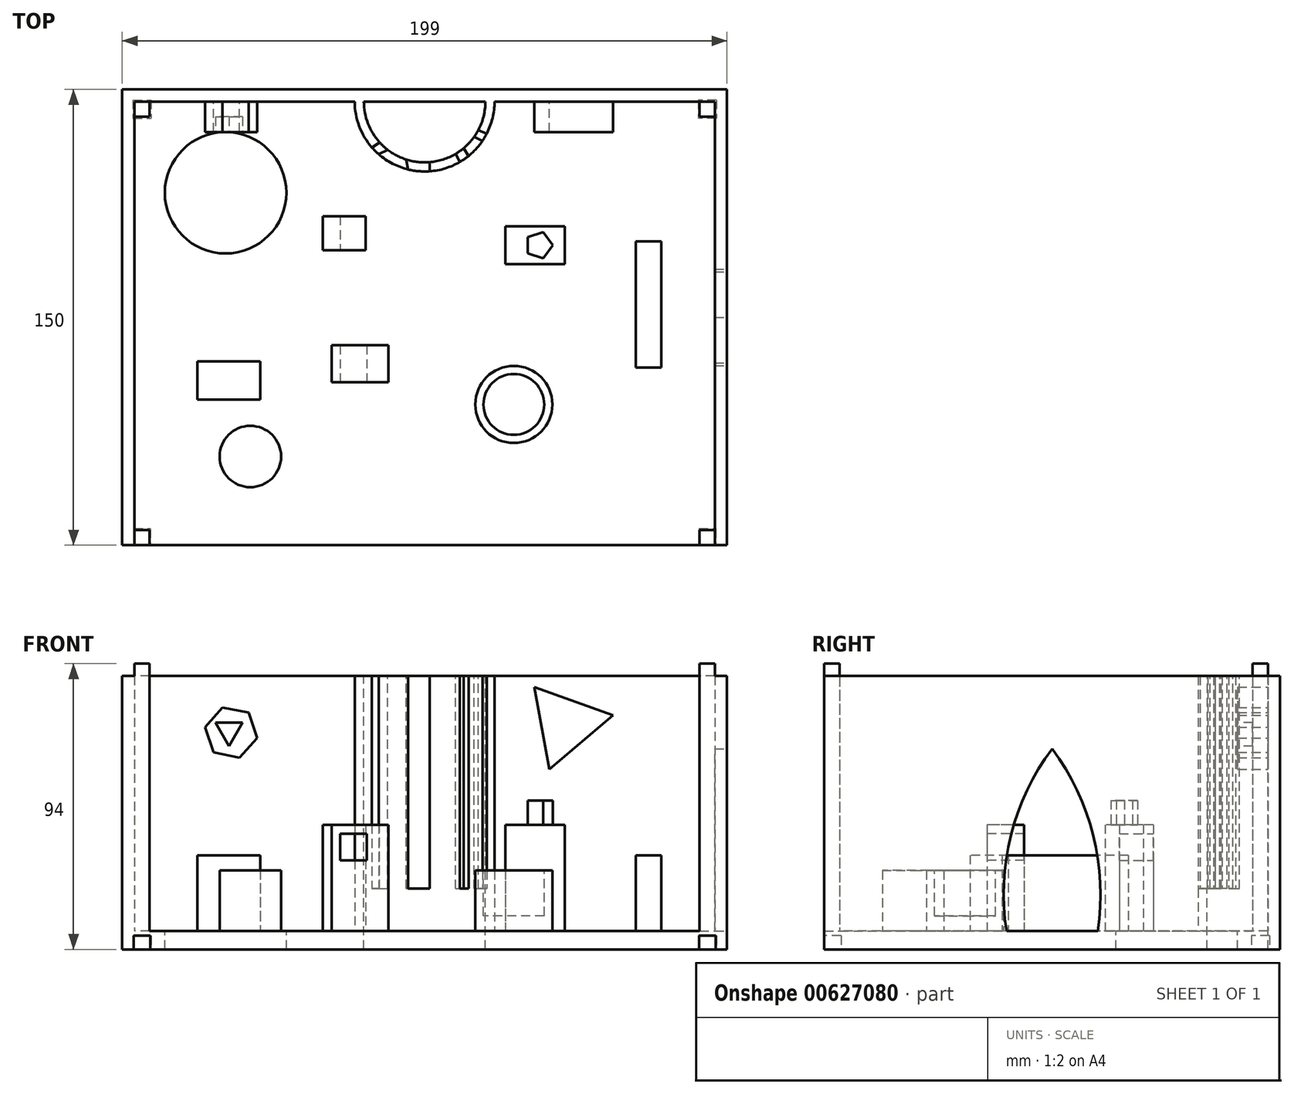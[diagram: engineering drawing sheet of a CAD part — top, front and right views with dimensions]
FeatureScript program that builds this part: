
annotation { "Feature Type Name" : "Feature", "Feature Type Description" : "" }
export const myFeature = defineFeature(function(context is Context, id is Id, definition is map)
    precondition{}
    {
        {
            var Q0;
            Q0=qCreatedBy(makeId("Top.planeOp"),FACE);
            var sketch = newSketch(context, id + "F0", { "sketchPlane" : qUnion([Q0])});
            skLineSegment(sketch, "E0.bottom", {"start": v(-99.5, 75) * mm, "end": v(99.5, 75) * mm});
            skLineSegment(sketch, "E0.top", {"start": v(-99.5, -75) * mm, "end": v(99.5, -75) * mm});
            skLineSegment(sketch, "E0.left", {"start": v(-99.5, 75) * mm, "end": v(-99.5, -75) * mm});
            skLineSegment(sketch, "E0.right", {"start": v(99.5, 75) * mm, "end": v(99.5, -75) * mm});
            skPoint(sketch, "E0.middle", {"position": v(0, 0) * mm});
            skPoint(sketch, "E1.orphan", {"position": v(-95.5, -75) * mm});
            skPoint(sketch, "E2.orphan", {"position": v(-99.5, -71) * mm});
            skPoint(sketch, "E3.orphan", {"position": v(95.5, -75) * mm});
            skPoint(sketch, "E4.orphan", {"position": v(99.5, 71) * mm});
            skPoint(sketch, "E5.orphan", {"position": v(-99.5, 71) * mm});
            skLineSegment(sketch, "E6", {"start": v(90.5, 71) * mm, "end": v(-90.5, 71) * mm});
            skLineSegment(sketch, "E7", {"start": v(-95.5, 66) * mm, "end": v(-95.5, -66) * mm});
            skLineSegment(sketch, "E8.MirrorCS", {"start": v(95.5, 66) * mm, "end": v(95.5, -66) * mm});
            skLineSegment(sketch, "E9", {"start": v(-90.5, 71) * mm, "end": v(-90.5, 66) * mm});
            skLineSegment(sketch, "E10", {"start": v(-90.5, 66) * mm, "end": v(-95.5, 66) * mm});
            skPoint(sketch, "E11.orphan", {"position": v(-95.5, 71) * mm});
            skLineSegment(sketch, "E12.MirrorCS", {"start": v(90.5, 71) * mm, "end": v(90.5, 66) * mm});
            skLineSegment(sketch, "E13.MirrorCS", {"start": v(90.5, 66) * mm, "end": v(95.5, 66) * mm});
            skLineSegment(sketch, "E14.trimOffspring", {"start": v(-95.5, -70) * mm, "end": v(-95.5, -75) * mm});
            skLineSegment(sketch, "E15.trimOffspring", {"start": v(95.5, -71) * mm, "end": v(95.5, -75) * mm});
            skPoint(sketch, "E16.orphan", {"position": v(95.5, 71) * mm});
            skLineSegment(sketch, "E17", {"start": v(-95.5, -75) * mm, "end": v(-90.5, -75) * mm});
            skLineSegment(sketch, "E18", {"start": v(-90.5, -75) * mm, "end": v(-90.5, -70) * mm});
            skLineSegment(sketch, "E19", {"start": v(-90.5, -70) * mm, "end": v(-95.5, -70) * mm});
            skLineSegment(sketch, "E20", {"start": v(-95.5, -66) * mm, "end": v(-95.5, -70) * mm});
            skLineSegment(sketch, "E21", {"start": v(-95.5, 66) * mm, "end": v(-95.5, 71) * mm});
            skLineSegment(sketch, "E22", {"start": v(-90.5, 71) * mm, "end": v(-95.5, 71) * mm});
            skLineSegment(sketch, "E23", {"start": v(90.5, 71) * mm, "end": v(95.5, 71) * mm});
            skLineSegment(sketch, "E24", {"start": v(95.5, 66) * mm, "end": v(95.5, 71) * mm});
            skLineSegment(sketch, "E25", {"start": v(95.5, -71) * mm, "end": v(95.5, -66) * mm});
            skLineSegment(sketch, "E26.MirrorCS", {"start": v(90.5, -70) * mm, "end": v(95.5, -70) * mm});
            skLineSegment(sketch, "E27.MirrorCS", {"start": v(90.5, -75) * mm, "end": v(90.5, -70) * mm});
            skSolve(sketch);
        }
        {
            var Q0;
            Q0=makeQuery(id+"F0.imprint","IMPRINT",FACE,{"disambiguationData":[TD([[makeQuery(id+"F0.imprint","IMPRINT",EDGE,{"derivedFrom":sQuery(id+"F0.wireOp",EDGE,"E6")}),1.0]])]});
            var Q1;
            Q1=makeQuery(id+"F0.imprint","IMPRINT",FACE,{"disambiguationData":[TD([[makeQuery(id+"F0.imprint","IMPRINT",EDGE,{"derivedFrom":sQuery(id+"F0.wireOp",EDGE,"E0.bottom")}),-1.0]])]});
            extrude(context, id + "F1", {"entities" : qUnion([Q0, Q1]), "depth" : 6 * mm, "offsetDistance" : 25 * mm});
        }
        {
            var Q0;
            Q0=makeQuery(id+"F0.imprint","IMPRINT",FACE,{"disambiguationData":[TD([[makeQuery(id+"F0.imprint","IMPRINT",EDGE,{"derivedFrom":sQuery(id+"F0.wireOp",EDGE,"E0.bottom")}),-1.0]])]});
            extrude(context, id + "F2", {"entities" : qUnion([Q0]), "operationType" : NewBodyOperationType.ADD, "depth" : 90 * mm, "offsetDistance" : 25 * mm});
        }
        {
            var Q0;
            Q0=makeQuery(id+"F0.imprint","IMPRINT",FACE,{"disambiguationData":[TD([[makeQuery(id+"F0.imprint","IMPRINT",EDGE,{"derivedFrom":sQuery(id+"F0.wireOp",EDGE,"E9")}),-1.0]])]});
            var Q1;
            Q1=makeQuery(id+"F0.imprint","IMPRINT",FACE,{"disambiguationData":[TD([[makeQuery(id+"F0.imprint","IMPRINT",EDGE,{"derivedFrom":sQuery(id+"F0.wireOp",EDGE,"E12.MirrorCS")}),1.0]])]});
            var Q2;
            {var subQ1=sQuery(id+"F0.wireOp",EDGE,"E15.trimOffspring");Q2=makeQuery(id+"F0.imprint","IMPRINT",FACE,{"disambiguationData":[TD([[makeQuery(id+"F0.imprint","IMPRINT",EDGE,{"derivedFrom":subQ1}),-1.0]])]});}
            var Q3;
            Q3=makeQuery(id+"F0.imprint","IMPRINT",FACE,{"disambiguationData":[TD([[makeQuery(id+"F0.imprint","IMPRINT",EDGE,{"derivedFrom":sQuery(id+"F0.wireOp",EDGE,"E14.trimOffspring")}),1.0]])]});
            extrude(context, id + "F3", {"entities" : qUnion([Q0, Q1, Q2, Q3]), "operationType" : NewBodyOperationType.ADD, "depth" : 94 * mm, "offsetDistance" : 25 * mm});
        }
        {
            var Q0;
            {var subQ0=sQuery(id+"F0.wireOp",EDGE,"E17");var subQ1=sQuery(id+"F0.wireOp",EDGE,"E0.top");var subQ2=makeQuery(id+"F0.imprint","IMPRINT",EDGE,{"disambiguationData":[TD([[makeQuery(id+"F0.imprint","INTERSECT",VERTEX,{"derivedFrom":[subQ1,sQuery(id+"F0.wireOp",EDGE,"E0.right")]}),1.0]])],"derivedFrom":subQ1});var subQ3=makeQuery(id+"F0.imprint","IMPRINT",EDGE,{"disambiguationData":[TD([[makeQuery(id+"F0.imprint","INTERSECT",VERTEX,{"derivedFrom":[subQ1,sQuery(id+"F0.wireOp",EDGE,"E0.left")]}),-1.0]])],"derivedFrom":subQ1});Q0=makeQuery(id+"F3.boolean.opBoolean","MERGE",FACE,{"derivedFrom":[makeQuery(id+"F1.opExtrude","SWEPT_FACE",FACE,{"disambiguationData":[OSD([subQ1]),TDD([makeQuery(id+"F0.imprint","IMPRINT",EDGE,{"disambiguationData":[TD([[makeQuery(id+"F0.imprint","INTERSECT",VERTEX,{"derivedFrom":[subQ1,sQuery(id+"F0.wireOp",EDGE,"E27.MirrorCS")]}),1.0]])],"derivedFrom":subQ1})])]}),makeQuery(id+"F2.boolean.opBoolean","MERGE",FACE,{"derivedFrom":[makeQuery(id+"F1.opExtrude","SWEPT_FACE",FACE,{"disambiguationData":[OSD([subQ1]),TDD([subQ3])]}),makeQuery(id+"F2.opExtrude","SWEPT_FACE",FACE,{"disambiguationData":[OSD([subQ1]),TDD([subQ3])]})]}),makeQuery(id+"F2.boolean.opBoolean","MERGE",FACE,{"derivedFrom":[makeQuery(id+"F1.opExtrude","SWEPT_FACE",FACE,{"disambiguationData":[OSD([subQ1]),TDD([subQ2])]}),makeQuery(id+"F2.opExtrude","SWEPT_FACE",FACE,{"disambiguationData":[OSD([subQ1]),TDD([subQ2])]})]}),makeQuery(id+"F3.opExtrude","SWEPT_FACE",FACE,{"disambiguationData":[OSD([subQ1])]}),makeQuery(id+"F3.opExtrude","SWEPT_FACE",FACE,{"disambiguationData":[OSD([subQ0])]})]});}
            var sketch = newSketch(context, id + "F4", { "sketchPlane" : qUnion([Q0])});
            skLineSegment(sketch, "E28", {"start": v(90.25, 4.5) * mm, "end": v(90.25, 0) * mm});
            skLineSegment(sketch, "E29", {"start": v(95.75, 4.5) * mm, "end": v(95.75, 0) * mm});
            skLineSegment(sketch, "E30", {"start": v(95.75, 0) * mm, "end": v(95.75, 4.5) * mm});
            skLineSegment(sketch, "E31", {"start": v(95.75, 4.5) * mm, "end": v(90.25, 4.5) * mm});
            skLineSegment(sketch, "E32", {"start": v(95.75, 0) * mm, "end": v(90.25, 0) * mm});
            skLineSegment(sketch, "E33.MirrorCS", {"start": v(-90.25, 4.5) * mm, "end": v(-90.25, 0) * mm});
            skLineSegment(sketch, "E34.MirrorCS", {"start": v(-95.75, 4.5) * mm, "end": v(-90.25, 4.5) * mm});
            skLineSegment(sketch, "E35.MirrorCS", {"start": v(-95.75, 0) * mm, "end": v(-90.25, 0) * mm});
            skLineSegment(sketch, "E36.MirrorCS", {"start": v(-95.75, 0) * mm, "end": v(-95.75, 4.5) * mm});
            skSolve(sketch);
        }
        {
            var Q0;
            Q0=makeQuery(id+"F4.imprint","IMPRINT",FACE,{"disambiguationData":[TD([[makeQuery(id+"F4.imprint","IMPRINT",EDGE,{"derivedFrom":sQuery(id+"F4.wireOp",EDGE,"E28")}),1.0]])]});
            extrude(context, id + "F5", {"entities" : qUnion([Q0]), "operationType" : NewBodyOperationType.REMOVE, "oppositeDirection" : true, "depth" : 5.5 * mm, "offsetDistance" : 25 * mm});
        }
        {
            var Q0;
            Q0=makeQuery(id+"F4.imprint","IMPRINT",FACE,{"disambiguationData":[TD([[makeQuery(id+"F4.imprint","IMPRINT",EDGE,{"derivedFrom":sQuery(id+"F4.wireOp",EDGE,"E33.MirrorCS")}),-1.0]])]});
            extrude(context, id + "F6", {"entities" : qUnion([Q0]), "operationType" : NewBodyOperationType.REMOVE, "depth" : 5.5 * mm, "offsetDistance" : 25 * mm});
        }
        {
            var Q0;
            Q0=makeQuery(id+"F1.opExtrude","CAP_FACE",FACE,{"disambiguationData":[OSD([sQuery(id+"F0.wireOp",EDGE,"E0.bottom"),sQuery(id+"F0.wireOp",EDGE,"E0.top"),sQuery(id+"F0.wireOp",EDGE,"E0.left"),sQuery(id+"F0.wireOp",EDGE,"E0.right"),sQuery(id+"F0.wireOp",EDGE,"E9"),sQuery(id+"F0.wireOp",EDGE,"E10"),sQuery(id+"F0.wireOp",EDGE,"E12.MirrorCS"),sQuery(id+"F0.wireOp",EDGE,"E13.MirrorCS"),sQuery(id+"F0.wireOp",EDGE,"E14.trimOffspring"),sQuery(id+"F0.wireOp",EDGE,"E15.trimOffspring"),sQuery(id+"F0.wireOp",EDGE,"E18"),sQuery(id+"F0.wireOp",EDGE,"E19"),sQuery(id+"F0.wireOp",EDGE,"E21"),sQuery(id+"F0.wireOp",EDGE,"E22"),sQuery(id+"F0.wireOp",EDGE,"E23"),sQuery(id+"F0.wireOp",EDGE,"E24"),sQuery(id+"F0.wireOp",EDGE,"E25"),sQuery(id+"F0.wireOp",EDGE,"E26.MirrorCS"),sQuery(id+"F0.wireOp",EDGE,"E27.MirrorCS")])],"isStart":false});
            var sketch = newSketch(context, id + "F7", { "sketchPlane" : qUnion([Q0])});
            skLineSegment(sketch, "E37", {"start": v(-90.5, 71) * mm, "end": v(-85.5, 71) * mm});
            skCircle(sketch, "E38", {"center": v(-65.5, 41) * mm, "radius": 20 * mm});
            skArc(sketch, "E39", {"start": v(-20, 71) * mm, "mid": v(0, 51) * mm, "end": v(20, 71) * mm});
            skLineSegment(sketch, "E40", {"start": v(20, 71) * mm, "end": v(-20, 71) * mm});
            skArc(sketch, "E41", {"start": v(-23, 71) * mm, "mid": v(0, 48) * mm, "end": v(23, 71) * mm});
            skLineSegment(sketch, "E42", {"start": v(23, 71) * mm, "end": v(-23, 71) * mm});
            skSolve(sketch);
        }
        {
            var Q0;
            Q0=makeQuery(id+"F7.imprint","IMPRINT",FACE,{"disambiguationData":[TD([[makeQuery(id+"F7.imprint","IMPRINT",EDGE,{"derivedFrom":sQuery(id+"F7.wireOp",EDGE,"E38")}),1.0]])]});
            extrude(context, id + "F8", {"entities" : qUnion([Q0]), "operationType" : NewBodyOperationType.REMOVE, "oppositeDirection" : true, "depth" : 7 * mm, "offsetDistance" : 25 * mm});
        }
        {
            var Q0;
            {var subQ0=sQuery(id+"F7.wireOp",EDGE,"E39");Q0=makeQuery(id+"F7.imprint","IMPRINT",FACE,{"disambiguationData":[TD([[makeQuery(id+"F7.imprint","IMPRINT",EDGE,{"derivedFrom":subQ0}),1.0]])]});}
            extrude(context, id + "F9", {"entities" : qUnion([Q0]), "operationType" : NewBodyOperationType.REMOVE, "oppositeDirection" : true, "depth" : 6 * mm, "offsetDistance" : 25 * mm});
        }
        {
            var Q0;
            {var subQ0=sQuery(id+"F7.wireOp",EDGE,"E39");Q0=makeQuery(id+"F7.imprint","IMPRINT",FACE,{"disambiguationData":[TD([[makeQuery(id+"F7.imprint","IMPRINT",EDGE,{"derivedFrom":subQ0}),-1.0]])]});}
            extrude(context, id + "F10", {"entities" : qUnion([Q0]), "operationType" : NewBodyOperationType.ADD, "depth" : 84 * mm, "offsetDistance" : 25 * mm});
        }
        {
            var Q0;
            {var subQ0=sQuery(id+"F0.wireOp",EDGE,"E0.right");Q0=makeQuery(id+"F2.boolean.opBoolean","MERGE",FACE,{"derivedFrom":[makeQuery(id+"F1.opExtrude","SWEPT_FACE",FACE,{"disambiguationData":[OSD([subQ0])]}),makeQuery(id+"F2.opExtrude","SWEPT_FACE",FACE,{"disambiguationData":[OSD([subQ0])]})]});}
            var sketch = newSketch(context, id + "F11", { "sketchPlane" : qUnion([Q0])});
            skLineSegment(sketch, "E43", {"start": v(14.97, 6) * mm, "end": v(-15.03, 6) * mm});
            skArc(sketch, "E44", {"start": v(-0.03, 66) * mm, "mid": v(-13.58, 37.51) * mm, "end": v(-15.03, 6) * mm});
            skArc(sketch, "E45.MirrorCS", {"start": v(-0.03, 66) * mm, "mid": v(13.52, 37.51) * mm, "end": v(14.97, 6) * mm});
            skSolve(sketch);
        }
        {
            var Q0;
            Q0=makeQuery(id+"F11.imprint","IMPRINT",FACE,{"disambiguationData":[TD([[makeQuery(id+"F11.imprint","IMPRINT",EDGE,{"derivedFrom":sQuery(id+"F11.wireOp",EDGE,"E43")}),-1.0]])]});
            extrude(context, id + "F12", {"entities" : qUnion([Q0]), "operationType" : NewBodyOperationType.REMOVE, "oppositeDirection" : true, "depth" : 4 * mm, "offsetDistance" : 25 * mm});
        }
        {
            var Q0;
            Q0=makeQuery(id+"F4.imprint","IMPRINT",FACE,{"disambiguationData":[TD([[makeQuery(id+"F4.imprint","IMPRINT",EDGE,{"derivedFrom":sQuery(id+"F4.wireOp",EDGE,"E33.MirrorCS")}),-1.0]])]});
            extrude(context, id + "F13", {"entities" : qUnion([Q0]), "operationType" : NewBodyOperationType.REMOVE, "oppositeDirection" : true, "depth" : 5.5 * mm, "offsetDistance" : 25 * mm});
        }
        {
            var Q0;
            Q0=makeQuery(id+"F0.imprint","IMPRINT",FACE,{"disambiguationData":[TD([[makeQuery(id+"F0.imprint","IMPRINT",EDGE,{"derivedFrom":sQuery(id+"F0.wireOp",EDGE,"E9")}),-1.0]])]});
            extrude(context, id + "F14", {"entities" : qUnion([Q0]), "operationType" : NewBodyOperationType.ADD, "depth" : 25 * mm, "offsetDistance" : 25 * mm});
        }
        {
            var Q0;
            {var subQ0=sQuery(id+"F0.wireOp",EDGE,"E19");var subQ1=sQuery(id+"F0.wireOp",EDGE,"E18");var subQ2=sQuery(id+"F0.wireOp",EDGE,"E14.trimOffspring");var subQ3=sQuery(id+"F0.wireOp",EDGE,"E24");var subQ4=sQuery(id+"F0.wireOp",EDGE,"E23");var subQ5=sQuery(id+"F0.wireOp",EDGE,"E13.MirrorCS");var subQ6=sQuery(id+"F0.wireOp",EDGE,"E12.MirrorCS");var subQ7=sQuery(id+"F0.wireOp",EDGE,"E22");var subQ8=sQuery(id+"F0.wireOp",EDGE,"E21");var subQ9=sQuery(id+"F0.wireOp",EDGE,"E10");var subQ10=sQuery(id+"F0.wireOp",EDGE,"E9");var subQ11=sQuery(id+"F0.wireOp",EDGE,"E27.MirrorCS");var subQ12=sQuery(id+"F0.wireOp",EDGE,"E26.MirrorCS");var subQ13=sQuery(id+"F0.wireOp",EDGE,"E25");var subQ14=sQuery(id+"F0.wireOp",EDGE,"E15.trimOffspring");var subQ15=sQuery(id+"F0.wireOp",EDGE,"E0.top");Q0=makeQuery(id+"F3.boolean.opBoolean","MERGE",FACE,{"derivedFrom":[makeQuery(id+"F1.opExtrude","CAP_FACE",FACE,{"disambiguationData":[OSD([sQuery(id+"F0.wireOp",EDGE,"E0.bottom"),subQ15,sQuery(id+"F0.wireOp",EDGE,"E0.left"),sQuery(id+"F0.wireOp",EDGE,"E0.right"),subQ10,subQ9,subQ6,subQ5,subQ2,subQ14,subQ1,subQ0,subQ8,subQ7,subQ4,subQ3,subQ13,subQ12,subQ11])],"isStart":true}),makeQuery(id+"F3.opExtrude","CAP_FACE",FACE,{"disambiguationData":[OSD([subQ15,subQ14,subQ13,subQ12,subQ11])],"isStart":true}),makeQuery(id+"F3.opExtrude","CAP_FACE",FACE,{"disambiguationData":[OSD([subQ10,subQ9,subQ8,subQ7])],"isStart":true}),makeQuery(id+"F3.opExtrude","CAP_FACE",FACE,{"disambiguationData":[OSD([subQ6,subQ5,subQ4,subQ3])],"isStart":true}),makeQuery(id+"F3.opExtrude","CAP_FACE",FACE,{"disambiguationData":[OSD([subQ2,sQuery(id+"F0.wireOp",EDGE,"E17"),subQ1,subQ0])],"isStart":true})]});}
            var sketch = newSketch(context, id + "F15", { "sketchPlane" : qUnion([Q0])});
            skLineSegment(sketch, "E46.0", {"start": v(-96, -71.49) * mm, "end": v(-96, -65.49) * mm});
            skLineSegment(sketch, "E46.1", {"start": v(-96, -71.49) * mm, "end": v(-90, -71.49) * mm});
            skLineSegment(sketch, "E46.2", {"start": v(-90, -71.49) * mm, "end": v(-90, -65.49) * mm});
            skLineSegment(sketch, "E46.3", {"start": v(-96, -65.49) * mm, "end": v(-90, -65.49) * mm});
            skSolve(sketch);
        }
        {
            var Q0;
            Q0=makeQuery(id+"F15.imprint","IMPRINT",FACE,{"disambiguationData":[TD([[makeQuery(id+"F15.imprint","IMPRINT",EDGE,{"derivedFrom":sQuery(id+"F15.wireOp",EDGE,"E46.0")}),-1.0]])]});
            extrude(context, id + "F16", {"entities" : qUnion([Q0]), "operationType" : NewBodyOperationType.REMOVE, "oppositeDirection" : true, "depth" : 4.5 * mm, "offsetDistance" : 25 * mm});
        }
        {
            var Q0;
            {var subQ0=sQuery(id+"F0.wireOp",EDGE,"E19");var subQ1=sQuery(id+"F0.wireOp",EDGE,"E18");var subQ2=sQuery(id+"F0.wireOp",EDGE,"E14.trimOffspring");var subQ3=sQuery(id+"F0.wireOp",EDGE,"E24");var subQ4=sQuery(id+"F0.wireOp",EDGE,"E23");var subQ5=sQuery(id+"F0.wireOp",EDGE,"E13.MirrorCS");var subQ6=sQuery(id+"F0.wireOp",EDGE,"E12.MirrorCS");var subQ7=sQuery(id+"F0.wireOp",EDGE,"E22");var subQ8=sQuery(id+"F0.wireOp",EDGE,"E21");var subQ9=sQuery(id+"F0.wireOp",EDGE,"E10");var subQ10=sQuery(id+"F0.wireOp",EDGE,"E9");var subQ11=sQuery(id+"F0.wireOp",EDGE,"E27.MirrorCS");var subQ12=sQuery(id+"F0.wireOp",EDGE,"E26.MirrorCS");var subQ13=sQuery(id+"F0.wireOp",EDGE,"E25");var subQ14=sQuery(id+"F0.wireOp",EDGE,"E15.trimOffspring");var subQ15=sQuery(id+"F0.wireOp",EDGE,"E0.top");Q0=makeQuery(id+"F3.boolean.opBoolean","MERGE",FACE,{"derivedFrom":[makeQuery(id+"F1.opExtrude","CAP_FACE",FACE,{"disambiguationData":[OSD([sQuery(id+"F0.wireOp",EDGE,"E0.bottom"),subQ15,sQuery(id+"F0.wireOp",EDGE,"E0.left"),sQuery(id+"F0.wireOp",EDGE,"E0.right"),subQ10,subQ9,subQ6,subQ5,subQ2,subQ14,subQ1,subQ0,subQ8,subQ7,subQ4,subQ3,subQ13,subQ12,subQ11])],"isStart":true}),makeQuery(id+"F3.opExtrude","CAP_FACE",FACE,{"disambiguationData":[OSD([subQ15,subQ14,subQ13,subQ12,subQ11])],"isStart":true}),makeQuery(id+"F3.opExtrude","CAP_FACE",FACE,{"disambiguationData":[OSD([subQ10,subQ9,subQ8,subQ7])],"isStart":true}),makeQuery(id+"F3.opExtrude","CAP_FACE",FACE,{"disambiguationData":[OSD([subQ6,subQ5,subQ4,subQ3])],"isStart":true}),makeQuery(id+"F3.opExtrude","CAP_FACE",FACE,{"disambiguationData":[OSD([subQ2,sQuery(id+"F0.wireOp",EDGE,"E17"),subQ1,subQ0])],"isStart":true})]});}
            var sketch = newSketch(context, id + "F17", { "sketchPlane" : qUnion([Q0])});
            skLineSegment(sketch, "E47.0", {"start": v(96, -65.5) * mm, "end": v(90, -65.5) * mm});
            skLineSegment(sketch, "E47.1", {"start": v(96, -71.5) * mm, "end": v(96, -65.5) * mm});
            skLineSegment(sketch, "E47.2", {"start": v(96, -71.5) * mm, "end": v(90, -71.5) * mm});
            skLineSegment(sketch, "E47.3", {"start": v(90, -71.5) * mm, "end": v(90, -65.5) * mm});
            skSolve(sketch);
        }
        {
            var Q0;
            Q0=makeQuery(id+"F17.imprint","IMPRINT",FACE,{"disambiguationData":[TD([[makeQuery(id+"F17.imprint","IMPRINT",EDGE,{"derivedFrom":sQuery(id+"F17.wireOp",EDGE,"E47.0")}),1.0]])]});
            extrude(context, id + "F18", {"entities" : qUnion([Q0]), "operationType" : NewBodyOperationType.REMOVE, "oppositeDirection" : true, "depth" : 4.5 * mm, "offsetDistance" : 25 * mm});
        }
        {
            var Q0;
            Q0=makeQuery(id+"F12.boolean.opBoolean","MERGE",FACE,{"derivedFrom":[makeQuery(id+"F1.opExtrude","CAP_FACE",FACE,{"disambiguationData":[OSD([sQuery(id+"F0.wireOp",EDGE,"E0.bottom"),sQuery(id+"F0.wireOp",EDGE,"E0.top"),sQuery(id+"F0.wireOp",EDGE,"E0.left"),sQuery(id+"F0.wireOp",EDGE,"E0.right"),sQuery(id+"F0.wireOp",EDGE,"E9"),sQuery(id+"F0.wireOp",EDGE,"E10"),sQuery(id+"F0.wireOp",EDGE,"E12.MirrorCS"),sQuery(id+"F0.wireOp",EDGE,"E13.MirrorCS"),sQuery(id+"F0.wireOp",EDGE,"E14.trimOffspring"),sQuery(id+"F0.wireOp",EDGE,"E15.trimOffspring"),sQuery(id+"F0.wireOp",EDGE,"E18"),sQuery(id+"F0.wireOp",EDGE,"E19"),sQuery(id+"F0.wireOp",EDGE,"E21"),sQuery(id+"F0.wireOp",EDGE,"E22"),sQuery(id+"F0.wireOp",EDGE,"E23"),sQuery(id+"F0.wireOp",EDGE,"E24"),sQuery(id+"F0.wireOp",EDGE,"E25"),sQuery(id+"F0.wireOp",EDGE,"E26.MirrorCS"),sQuery(id+"F0.wireOp",EDGE,"E27.MirrorCS")])],"isStart":false}),makeQuery(id+"F12.opExtrude","SWEPT_FACE",FACE,{"disambiguationData":[OSD([sQuery(id+"F11.wireOp",EDGE,"E43")])]})]});
            var sketch = newSketch(context, id + "F19", { "sketchPlane" : qUnion([Q0])});
            skLineSegment(sketch, "E48.bottom", {"start": v(26.55, 29.99) * mm, "end": v(46.13, 29.99) * mm});
            skLineSegment(sketch, "E48.top", {"start": v(26.55, 17.47) * mm, "end": v(46.13, 17.47) * mm});
            skLineSegment(sketch, "E48.left", {"start": v(26.55, 29.99) * mm, "end": v(26.55, 17.47) * mm});
            skLineSegment(sketch, "E48.right", {"start": v(46.13, 29.99) * mm, "end": v(46.13, 17.47) * mm});
            skLineSegment(sketch, "E49.bottom", {"start": v(-30.54, -9.23) * mm, "end": v(-11.9, -9.23) * mm});
            skLineSegment(sketch, "E49.top", {"start": v(-30.54, -21.42) * mm, "end": v(-11.9, -21.42) * mm});
            skLineSegment(sketch, "E49.left", {"start": v(-30.54, -9.23) * mm, "end": v(-30.54, -21.42) * mm});
            skLineSegment(sketch, "E49.right", {"start": v(-11.9, -9.23) * mm, "end": v(-11.9, -21.42) * mm});
            skLineSegment(sketch, "E50.bottom", {"start": v(-33.57, 33.29) * mm, "end": v(-19.36, 33.29) * mm});
            skLineSegment(sketch, "E50.top", {"start": v(-33.57, 22.08) * mm, "end": v(-19.36, 22.08) * mm});
            skLineSegment(sketch, "E50.left", {"start": v(-33.57, 33.29) * mm, "end": v(-33.57, 22.08) * mm});
            skLineSegment(sketch, "E50.right", {"start": v(-19.36, 33.29) * mm, "end": v(-19.36, 22.08) * mm});
            skLineSegment(sketch, "E51.bottom", {"start": v(-74.82, -14.5) * mm, "end": v(-54.08, -14.5) * mm});
            skLineSegment(sketch, "E51.top", {"start": v(-74.82, -27.02) * mm, "end": v(-54.08, -27.02) * mm});
            skLineSegment(sketch, "E51.left", {"start": v(-74.82, -14.5) * mm, "end": v(-74.82, -27.02) * mm});
            skLineSegment(sketch, "E51.right", {"start": v(-54.08, -14.5) * mm, "end": v(-54.08, -27.02) * mm});
            skLineSegment(sketch, "E52.bottom", {"start": v(69.43, 25.05) * mm, "end": v(77.82, 25.05) * mm});
            skLineSegment(sketch, "E52.top", {"start": v(69.43, -16.48) * mm, "end": v(77.82, -16.48) * mm});
            skLineSegment(sketch, "E52.left", {"start": v(69.43, 25.05) * mm, "end": v(69.43, -16.48) * mm});
            skLineSegment(sketch, "E52.right", {"start": v(77.82, 25.05) * mm, "end": v(77.82, -16.48) * mm});
            skSolve(sketch);
        }
        {
            var Q0;
            Q0=makeQuery(id+"F19.imprint","IMPRINT",FACE,{"disambiguationData":[TD([[makeQuery(id+"F19.imprint","IMPRINT",EDGE,{"derivedFrom":sQuery(id+"F19.wireOp",EDGE,"E51.bottom")}),-1.0]])]});
            var Q1;
            Q1=makeQuery(id+"F19.imprint","IMPRINT",FACE,{"disambiguationData":[TD([[makeQuery(id+"F19.imprint","IMPRINT",EDGE,{"derivedFrom":sQuery(id+"F19.wireOp",EDGE,"E52.bottom")}),-1.0]])]});
            extrude(context, id + "F20", {"entities" : qUnion([Q0, Q1]), "operationType" : NewBodyOperationType.ADD, "depth" : 25 * mm, "offsetDistance" : 25 * mm});
        }
        {
            var Q0;
            Q0=makeQuery(id+"F19.imprint","IMPRINT",FACE,{"disambiguationData":[TD([[makeQuery(id+"F19.imprint","IMPRINT",EDGE,{"derivedFrom":sQuery(id+"F19.wireOp",EDGE,"E50.bottom")}),-1.0]])]});
            var Q1;
            Q1=makeQuery(id+"F19.imprint","IMPRINT",FACE,{"disambiguationData":[TD([[makeQuery(id+"F19.imprint","IMPRINT",EDGE,{"derivedFrom":sQuery(id+"F19.wireOp",EDGE,"E49.bottom")}),-1.0]])]});
            var Q2;
            Q2=makeQuery(id+"F19.imprint","IMPRINT",FACE,{"disambiguationData":[TD([[makeQuery(id+"F19.imprint","IMPRINT",EDGE,{"derivedFrom":sQuery(id+"F19.wireOp",EDGE,"E48.bottom")}),-1.0]])]});
            extrude(context, id + "F21", {"entities" : qUnion([Q0, Q1, Q2]), "operationType" : NewBodyOperationType.ADD, "depth" : 35 * mm, "offsetDistance" : 25 * mm});
        }
        {
            var Q0;
            Q0=makeQuery(id+"F19.imprint","IMPRINT",FACE,{"disambiguationData":[TD([[makeQuery(id+"F19.imprint","IMPRINT",EDGE,{"derivedFrom":sQuery(id+"F19.wireOp",EDGE,"E48.bottom")}),1.0]])]});
            var sketch = newSketch(context, id + "F22", { "sketchPlane" : qUnion([Q0])});
            skCircle(sketch, "E53", {"center": v(29.35, -28.67) * mm, "radius": 12.68 * mm});
            skCircle(sketch, "E54", {"center": v(-57.34, -45.8) * mm, "radius": 10.1 * mm});
            skSolve(sketch);
        }
        {
            var Q0;
            Q0 = qSketchRegion(id + "F22", true);
            extrude(context, id + "F23", {"entities" : qUnion([Q0]), "operationType" : NewBodyOperationType.ADD, "depth" : 20 * mm, "offsetDistance" : 25 * mm});
        }
        {
            var Q0;
            {var subQ0=sQuery(id+"F0.wireOp",EDGE,"E12.MirrorCS");var subQ1=sQuery(id+"F0.wireOp",EDGE,"E23");var subQ4=sQuery(id+"F0.wireOp",EDGE,"E22");var subQ8=sQuery(id+"F0.wireOp",EDGE,"E6");var subQ14=sQuery(id+"F7.wireOp",EDGE,"E42");Q0=makeQuery(id+"F10.boolean.opBoolean","SPLIT",FACE,{"disambiguationData":[TD([makeQuery(id+"F3.opExtrude","SWEPT_FACE",FACE,{"disambiguationData":[OSD([subQ0])]})])],"derivedFrom":makeQuery(id+"F9.boolean.opBoolean","MERGE",FACE,{"derivedFrom":[makeQuery(id+"F2.boolean.opBoolean","MERGE",FACE,{"derivedFrom":[makeQuery(id+"F1.opExtrude","SWEPT_FACE",FACE,{"disambiguationData":[OSD([subQ4])]}),makeQuery(id+"F1.opExtrude","SWEPT_FACE",FACE,{"disambiguationData":[OSD([subQ1])]}),makeQuery(id+"F2.opExtrude","SWEPT_FACE",FACE,{"disambiguationData":[OSD([subQ8,subQ4,subQ1])]})]}),makeQuery(id+"F9.opExtrude","SWEPT_FACE",FACE,{"disambiguationData":[OSD([subQ14])]})]})});}
            var sketch = newSketch(context, id + "F24", { "sketchPlane" : qUnion([Q0])});
            skCircle(sketch, "E55.cCircle", {"center": v(46.36, 74.17) * mm, "radius": 7.94 * mm, "construction": true});
            skLineSegment(sketch, "E55.0", {"start": v(61.98, 77) * mm, "end": v(41, 59.23) * mm});
            skLineSegment(sketch, "E55.1", {"start": v(41, 59.23) * mm, "end": v(36.1, 86.29) * mm});
            skLineSegment(sketch, "E55.2", {"start": v(36.1, 86.29) * mm, "end": v(61.98, 77) * mm});
            skPoint(sketch, "E55.0.midPoint", {"position": v(51.49, 68.11) * mm});
            skSolve(sketch);
        }
        {
            var Q0;
            Q0=makeQuery(id+"F24.imprint","IMPRINT",FACE,{"disambiguationData":[TD([[makeQuery(id+"F24.imprint","IMPRINT",EDGE,{"derivedFrom":sQuery(id+"F24.wireOp",EDGE,"E55.0")}),-1.0]])]});
            extrude(context, id + "F25", {"entities" : qUnion([Q0]), "operationType" : NewBodyOperationType.ADD, "depth" : 10 * mm, "offsetDistance" : 25 * mm});
        }
        {
            var Q0;
            Q0=makeQuery(id+"F23.opExtrude","CAP_FACE",FACE,{"disambiguationData":[OSD([sQuery(id+"F22.wireOp",EDGE,"E53")])],"isStart":false});
            var sketch = newSketch(context, id + "F26", { "sketchPlane" : qUnion([Q0])});
            skCircle(sketch, "E56", {"center": v(29.35, -28.67) * mm, "radius": 10 * mm});
            skSolve(sketch);
        }
        {
            var Q0;
            Q0 = qSketchRegion(id + "F26", true);
            extrude(context, id + "F27", {"entities" : qUnion([Q0]), "operationType" : NewBodyOperationType.REMOVE, "oppositeDirection" : true, "depth" : 15 * mm, "offsetDistance" : 25 * mm});
        }
        {
            var Q0;
            Q0=makeQuery(id+"F21.opExtrude","SWEPT_FACE",FACE,{"disambiguationData":[OSD([sQuery(id+"F19.wireOp",EDGE,"E49.top")])]});
            var sketch = newSketch(context, id + "F28", { "sketchPlane" : qUnion([Q0])});
            skLineSegment(sketch, "E57.bottom", {"start": v(-27.77, 38.02) * mm, "end": v(-19.06, 38.02) * mm});
            skLineSegment(sketch, "E57.top", {"start": v(-27.77, 29.3) * mm, "end": v(-19.06, 29.3) * mm});
            skLineSegment(sketch, "E57.left", {"start": v(-27.77, 38.02) * mm, "end": v(-27.77, 29.3) * mm});
            skLineSegment(sketch, "E57.right", {"start": v(-19.06, 38.02) * mm, "end": v(-19.06, 29.3) * mm});
            skSolve(sketch);
        }
        {
            var Q0;
            Q0 = qSketchRegion(id + "F28", true);
            extrude(context, id + "F29", {"entities" : qUnion([Q0]), "operationType" : NewBodyOperationType.REMOVE, "oppositeDirection" : true, "depth" : 55 * mm, "offsetDistance" : 25 * mm});
        }
        {
            var Q0;
            {var subQ0=sQuery(id+"F0.wireOp",EDGE,"E9");var subQ3=sQuery(id+"F0.wireOp",EDGE,"E23");var subQ4=sQuery(id+"F0.wireOp",EDGE,"E22");var subQ8=sQuery(id+"F0.wireOp",EDGE,"E6");var subQ14=sQuery(id+"F7.wireOp",EDGE,"E42");Q0=makeQuery(id+"F10.boolean.opBoolean","SPLIT",FACE,{"disambiguationData":[TD([makeQuery(id+"F3.opExtrude","SWEPT_FACE",FACE,{"disambiguationData":[OSD([subQ0])]})])],"derivedFrom":makeQuery(id+"F9.boolean.opBoolean","MERGE",FACE,{"derivedFrom":[makeQuery(id+"F2.boolean.opBoolean","MERGE",FACE,{"derivedFrom":[makeQuery(id+"F1.opExtrude","SWEPT_FACE",FACE,{"disambiguationData":[OSD([subQ4])]}),makeQuery(id+"F1.opExtrude","SWEPT_FACE",FACE,{"disambiguationData":[OSD([subQ3])]}),makeQuery(id+"F2.opExtrude","SWEPT_FACE",FACE,{"disambiguationData":[OSD([subQ8,subQ4,subQ3])]})]}),makeQuery(id+"F9.opExtrude","SWEPT_FACE",FACE,{"disambiguationData":[OSD([subQ14])]})]})});}
            var sketch = newSketch(context, id + "F30", { "sketchPlane" : qUnion([Q0])});
            skCircle(sketch, "E58.cCircle", {"center": v(-63.72, 71.35) * mm, "radius": 7.56 * mm, "construction": true});
            skLineSegment(sketch, "E58.0", {"start": v(-55.16, 69.6) * mm, "end": v(-60.95, 63.07) * mm});
            skLineSegment(sketch, "E58.1", {"start": v(-60.95, 63.07) * mm, "end": v(-69.5, 64.8) * mm});
            skLineSegment(sketch, "E58.2", {"start": v(-69.5, 64.8) * mm, "end": v(-72.28, 73.09) * mm});
            skLineSegment(sketch, "E58.3", {"start": v(-72.28, 73.09) * mm, "end": v(-66.5, 79.63) * mm});
            skLineSegment(sketch, "E58.4", {"start": v(-66.5, 79.63) * mm, "end": v(-57.93, 77.89) * mm});
            skLineSegment(sketch, "E58.5", {"start": v(-57.93, 77.89) * mm, "end": v(-55.16, 69.6) * mm});
            skPoint(sketch, "E58.0.midPoint", {"position": v(-58.05, 66.34) * mm});
            skSolve(sketch);
        }
        {
            var Q0;
            Q0 = qSketchRegion(id + "F30", true);
            extrude(context, id + "F31", {"entities" : qUnion([Q0]), "operationType" : NewBodyOperationType.ADD, "depth" : 10 * mm, "offsetDistance" : 25 * mm});
        }
        {
            var Q0;
            Q0=makeQuery(id+"F21.opExtrude","CAP_FACE",FACE,{"disambiguationData":[OSD([sQuery(id+"F19.wireOp",EDGE,"E48.bottom"),sQuery(id+"F19.wireOp",EDGE,"E48.top"),sQuery(id+"F19.wireOp",EDGE,"E48.left"),sQuery(id+"F19.wireOp",EDGE,"E48.right")])],"isStart":false});
            var sketch = newSketch(context, id + "F32", { "sketchPlane" : qUnion([Q0])});
            skCircle(sketch, "E59.cCircle", {"center": v(37.58, 23.73) * mm, "radius": 3.7 * mm, "construction": true});
            skPoint(sketch, "E59.cCircle.centerSnap0", {"position": v(46.13, 23.73) * mm});
            skLineSegment(sketch, "E59.0", {"start": v(33.87, 21.04) * mm, "end": v(33.87, 26.42) * mm});
            skLineSegment(sketch, "E59.1", {"start": v(33.87, 26.42) * mm, "end": v(39, 28.08) * mm});
            skLineSegment(sketch, "E59.2", {"start": v(39, 28.08) * mm, "end": v(42.16, 23.73) * mm});
            skLineSegment(sketch, "E59.3", {"start": v(42.16, 23.73) * mm, "end": v(39, 19.37) * mm});
            skLineSegment(sketch, "E59.4", {"start": v(39, 19.37) * mm, "end": v(33.87, 21.04) * mm});
            skPoint(sketch, "E59.0.midPoint", {"position": v(33.87, 23.73) * mm});
            skSolve(sketch);
        }
        {
            var Q0;
            Q0=makeQuery(id+"F32.imprint","IMPRINT",FACE,{"disambiguationData":[TD([[makeQuery(id+"F32.imprint","IMPRINT",EDGE,{"derivedFrom":sQuery(id+"F32.wireOp",EDGE,"E59.0")}),-1.0]])]});
            extrude(context, id + "F33", {"entities" : qUnion([Q0]), "operationType" : NewBodyOperationType.ADD, "depth" : 8 * mm, "offsetDistance" : 25 * mm});
        }
        {
            var Q0;
            Q0=makeQuery(id+"F31.opExtrude","CAP_FACE",FACE,{"disambiguationData":[OSD([sQuery(id+"F30.wireOp",EDGE,"E58.0"),sQuery(id+"F30.wireOp",EDGE,"E58.1"),sQuery(id+"F30.wireOp",EDGE,"E58.2"),sQuery(id+"F30.wireOp",EDGE,"E58.3"),sQuery(id+"F30.wireOp",EDGE,"E58.4"),sQuery(id+"F30.wireOp",EDGE,"E58.5")])],"isStart":false});
            var sketch = newSketch(context, id + "F34", { "sketchPlane" : qUnion([Q0])});
            skCircle(sketch, "E60.cCircle", {"center": v(-64.37, 72) * mm, "radius": 2.6 * mm, "construction": true});
            skLineSegment(sketch, "E60.0", {"start": v(-68.86, 74.6) * mm, "end": v(-59.89, 74.6) * mm});
            skLineSegment(sketch, "E60.1", {"start": v(-59.89, 74.6) * mm, "end": v(-64.37, 66.82) * mm});
            skLineSegment(sketch, "E60.2", {"start": v(-64.37, 66.82) * mm, "end": v(-68.86, 74.6) * mm});
            skPoint(sketch, "E60.0.midPoint", {"position": v(-64.37, 74.6) * mm});
            skSolve(sketch);
        }
        {
            var Q0;
            Q0 = qSketchRegion(id + "F34", true);
            extrude(context, id + "F35", {"entities" : qUnion([Q0]), "operationType" : NewBodyOperationType.REMOVE, "oppositeDirection" : true, "depth" : 5 * mm, "offsetDistance" : 25 * mm});
        }
        {
            var Q0;
            Q0=makeQuery(id+"F10.boolean.opBoolean","MERGE",FACE,{"derivedFrom":[makeQuery(id+"F2.opExtrude","CAP_FACE",FACE,{"disambiguationData":[OSD([sQuery(id+"F0.wireOp",EDGE,"E0.bottom"),sQuery(id+"F0.wireOp",EDGE,"E0.top"),sQuery(id+"F0.wireOp",EDGE,"E0.left"),sQuery(id+"F0.wireOp",EDGE,"E0.right"),sQuery(id+"F0.wireOp",EDGE,"E6"),sQuery(id+"F0.wireOp",EDGE,"E7"),sQuery(id+"F0.wireOp",EDGE,"E8.MirrorCS"),sQuery(id+"F0.wireOp",EDGE,"E14.trimOffspring"),sQuery(id+"F0.wireOp",EDGE,"E15.trimOffspring"),sQuery(id+"F0.wireOp",EDGE,"E20"),sQuery(id+"F0.wireOp",EDGE,"E21"),sQuery(id+"F0.wireOp",EDGE,"E22"),sQuery(id+"F0.wireOp",EDGE,"E23"),sQuery(id+"F0.wireOp",EDGE,"E24"),sQuery(id+"F0.wireOp",EDGE,"E25")])],"isStart":false}),makeQuery(id+"F10.opExtrude","CAP_FACE",FACE,{"disambiguationData":[OSD([sQuery(id+"F7.wireOp",EDGE,"E39"),sQuery(id+"F7.wireOp",EDGE,"E41"),sQuery(id+"F7.wireOp",EDGE,"E42")])],"isStart":false})]});
            var sketch = newSketch(context, id + "F36", { "sketchPlane" : qUnion([Q0])});
            skLineSegment(sketch, "E61", {"start": v(-6.5, 54.1) * mm, "end": v(-4.96, 46.55) * mm});
            skLineSegment(sketch, "E62", {"start": v(-4.96, 46.55) * mm, "end": v(1.66, 46.55) * mm});
            skLineSegment(sketch, "E63", {"start": v(1.66, 46.55) * mm, "end": v(1.66, 54.87) * mm});
            skLineSegment(sketch, "E64", {"start": v(1.66, 54.87) * mm, "end": v(-6.5, 54.1) * mm});
            skLineSegment(sketch, "E65", {"start": v(9.67, 54.64) * mm, "end": v(12.3, 49.87) * mm});
            skLineSegment(sketch, "E66", {"start": v(12.3, 49.87) * mm, "end": v(15.4, 51.57) * mm});
            skLineSegment(sketch, "E67", {"start": v(15.4, 51.57) * mm, "end": v(11.99, 56.95) * mm});
            skLineSegment(sketch, "E68", {"start": v(11.99, 56.95) * mm, "end": v(9.67, 54.64) * mm});
            skLineSegment(sketch, "E69", {"start": v(-13.82, 58.18) * mm, "end": v(-18.6, 55.03) * mm});
            skLineSegment(sketch, "E70", {"start": v(-18.6, 55.03) * mm, "end": v(-16.13, 53.18) * mm});
            skLineSegment(sketch, "E71", {"start": v(-16.13, 53.18) * mm, "end": v(-10.5, 55.87) * mm});
            skLineSegment(sketch, "E72", {"start": v(-10.5, 55.87) * mm, "end": v(-13.82, 58.18) * mm});
            skLineSegment(sketch, "E73", {"start": v(16.3, 59.42) * mm, "end": v(20.3, 57.41) * mm});
            skLineSegment(sketch, "E74", {"start": v(20.3, 57.41) * mm, "end": v(21.56, 59.9) * mm});
            skLineSegment(sketch, "E75", {"start": v(21.56, 59.9) * mm, "end": v(16.84, 61.96) * mm});
            skLineSegment(sketch, "E76", {"start": v(16.84, 61.96) * mm, "end": v(16.3, 59.42) * mm});
            skSolve(sketch);
        }
        {
            var Q0;
            Q0 = qSketchRegion(id + "F36", true);
            extrude(context, id + "F37", {"entities" : qUnion([Q0]), "operationType" : NewBodyOperationType.REMOVE, "oppositeDirection" : true, "depth" : 70 * mm, "offsetDistance" : 25 * mm});
        }
    });
